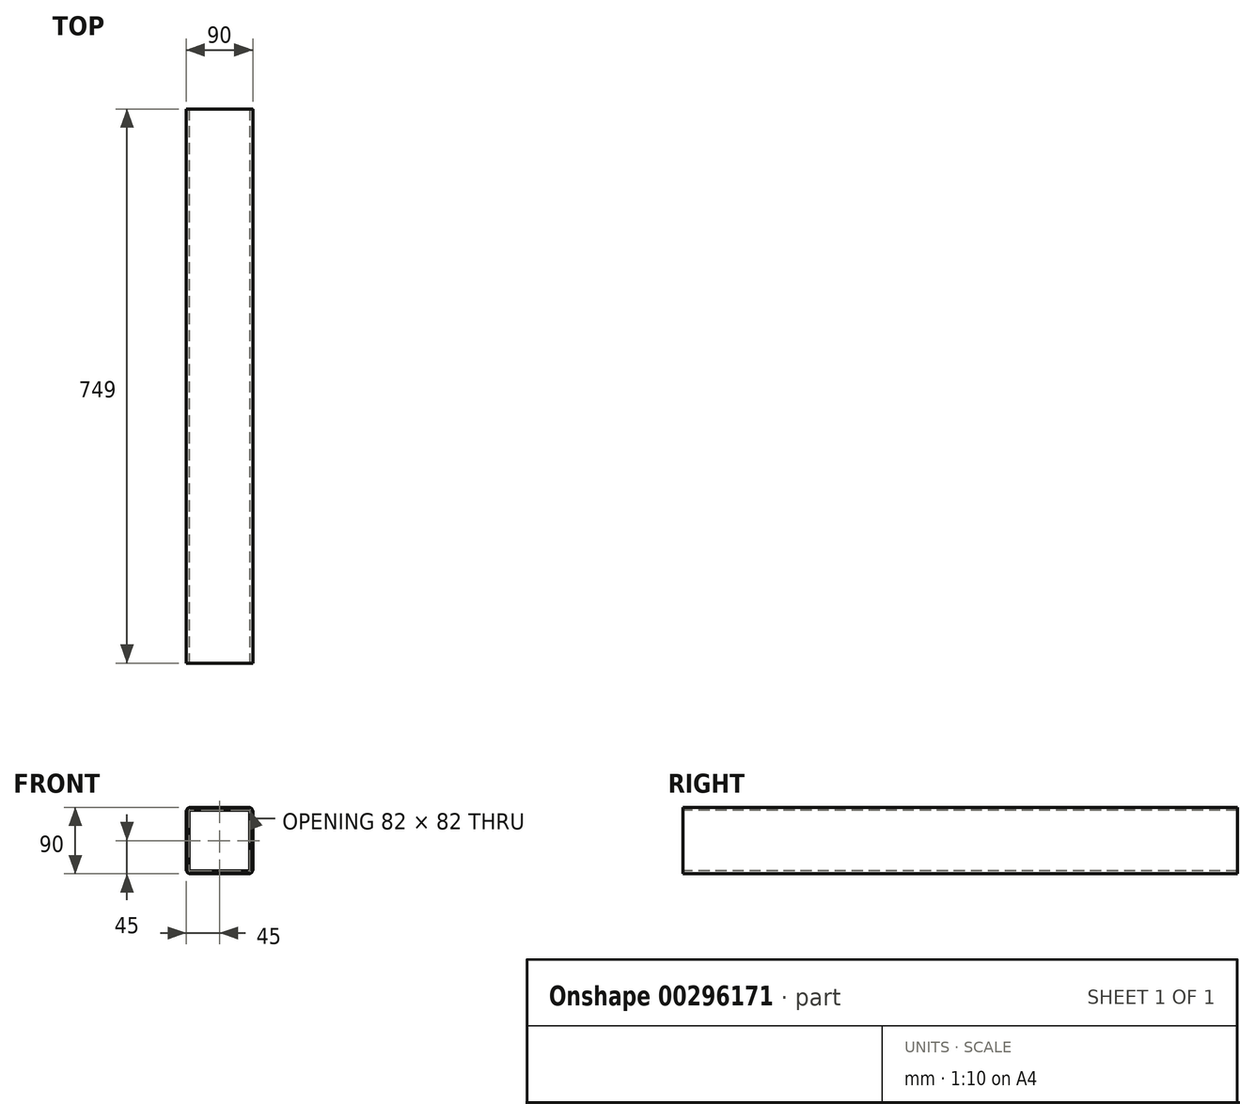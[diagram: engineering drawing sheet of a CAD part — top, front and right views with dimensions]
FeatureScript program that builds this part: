
annotation { "Feature Type Name" : "Feature", "Feature Type Description" : "" }
export const myFeature = defineFeature(function(context is Context, id is Id, definition is map)
    precondition{}
    {
        {
            var Q0;
            Q0=qCreatedBy(makeId("Front.planeOp"),FACE);
            var sketch = newSketch(context, id + "F0", { "sketchPlane" : qUnion([Q0])});
            skLineSegment(sketch, "E0.bottom", {"start": v(39, 45) * mm, "end": v(-39, 45) * mm});
            skLineSegment(sketch, "E0.top", {"start": v(39, -45) * mm, "end": v(-39, -45) * mm});
            skLineSegment(sketch, "E0.left", {"start": v(45, 39) * mm, "end": v(45, -39) * mm});
            skLineSegment(sketch, "E0.right", {"start": v(-45, 39) * mm, "end": v(-45, -39) * mm});
            skPoint(sketch, "E0.middle", {"position": v(0, 0) * mm});
            skPoint(sketch, "E1.visualSharp", {"position": v(-45, 45) * mm});
            skArc(sketch, "E1.filletArc", {"start": v(-39, 45) * mm, "mid": v(-43.24, 43.24) * mm, "end": v(-45, 39) * mm});
            skPoint(sketch, "E2.visualSharp", {"position": v(45, 45) * mm});
            skArc(sketch, "E2.filletArc", {"start": v(45, 39) * mm, "mid": v(43.24, 43.24) * mm, "end": v(39, 45) * mm});
            skPoint(sketch, "E3.visualSharp", {"position": v(45, -45) * mm});
            skArc(sketch, "E3.filletArc", {"start": v(39, -45) * mm, "mid": v(43.24, -43.24) * mm, "end": v(45, -39) * mm});
            skPoint(sketch, "E4.visualSharp", {"position": v(-45, -45) * mm});
            skArc(sketch, "E4.filletArc", {"start": v(-45, -39) * mm, "mid": v(-43.24, -43.24) * mm, "end": v(-39, -45) * mm});
            skArc(sketch, "E5.0", {"start": v(-39, 41) * mm, "mid": v(-40.41, 40.41) * mm, "end": v(-41, 39) * mm});
            skLineSegment(sketch, "E5.1", {"start": v(39, 41) * mm, "end": v(-39, 41) * mm});
            skLineSegment(sketch, "E5.2", {"start": v(-41, 39) * mm, "end": v(-41, -39) * mm});
            skArc(sketch, "E5.3", {"start": v(41, 39) * mm, "mid": v(40.41, 40.41) * mm, "end": v(39, 41) * mm});
            skArc(sketch, "E5.4", {"start": v(-41, -39) * mm, "mid": v(-40.41, -40.41) * mm, "end": v(-39, -41) * mm});
            skLineSegment(sketch, "E5.5", {"start": v(39, -41) * mm, "end": v(-39, -41) * mm});
            skArc(sketch, "E5.6", {"start": v(39, -41) * mm, "mid": v(40.41, -40.41) * mm, "end": v(41, -39) * mm});
            skLineSegment(sketch, "E5.7", {"start": v(41, 39) * mm, "end": v(41, -39) * mm});
            skSolve(sketch);
        }
        {
            var Q0;
            Q0=makeQuery(id+"F0.imprint","IMPRINT",FACE,{"disambiguationData":[TD([[makeQuery(id+"F0.imprint","IMPRINT",EDGE,{"derivedFrom":sQuery(id+"F0.wireOp",EDGE,"E0.bottom")}),1.0]])]});
            extrude(context, id + "F1", {"entities" : qUnion([Q0]), "oppositeDirection" : true, "depth" : 749 * mm});
        }
    });
